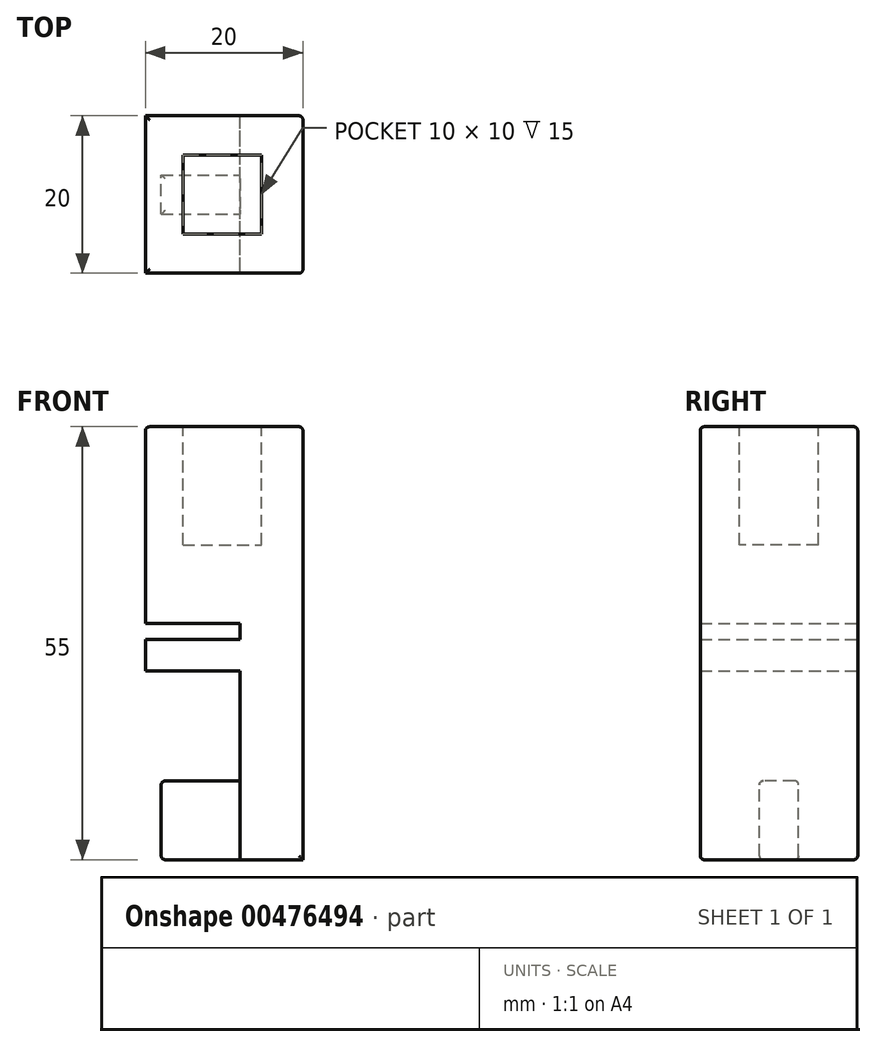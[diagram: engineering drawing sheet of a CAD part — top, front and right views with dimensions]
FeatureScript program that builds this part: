
annotation { "Feature Type Name" : "Feature", "Feature Type Description" : "" }
export const myFeature = defineFeature(function(context is Context, id is Id, definition is map)
    precondition{}
    {
        {
            var Q0;
            Q0=qCreatedBy(makeId("Front.planeOp"),FACE);
            var sketch = newSketch(context, id + "F0", { "sketchPlane" : qUnion([Q0])});
            skLineSegment(sketch, "E0.bottom", {"start": v(-17.88, 11) * mm, "end": v(2.12, 11) * mm});
            skLineSegment(sketch, "E0.top", {"start": v(-17.88, -24) * mm, "end": v(2.12, -24) * mm});
            skLineSegment(sketch, "E0.left", {"start": v(-17.88, 11) * mm, "end": v(-17.88, -24) * mm});
            skLineSegment(sketch, "E0.right", {"start": v(2.12, 11) * mm, "end": v(2.12, -24) * mm});
            skLineSegment(sketch, "E1", {"start": v(-17.88, 6) * mm, "end": v(2.12, 6) * mm});
            skLineSegment(sketch, "E2", {"start": v(-5.88, 6) * mm, "end": v(-5.88, -24) * mm});
            skLineSegment(sketch, "E3", {"start": v(-5.88, 4) * mm, "end": v(-17.88, 4) * mm});
            skLineSegment(sketch, "E4", {"start": v(-17.88, 0) * mm, "end": v(-5.88, 0) * mm});
            skLineSegment(sketch, "E5", {"start": v(-17.88, -14) * mm, "end": v(-5.88, -14) * mm});
            skSolve(sketch);
        }
        {
            var Q0;
            {var subQ1=sQuery(id+"F0.wireOp",EDGE,"E0.bottom");Q0=makeQuery(id+"F0.imprint","IMPRINT",FACE,{"disambiguationData":[TD([[makeQuery(id+"F0.imprint","IMPRINT",EDGE,{"derivedFrom":subQ1}),-1.0]])]});}
            var Q1;
            {var subQ1=sQuery(id+"F0.wireOp",EDGE,"E0.right");var subQ5=sQuery(id+"F0.wireOp",EDGE,"E0.top");var subQ6=makeQuery(id+"F0.imprint","INTERSECT",VERTEX,{"derivedFrom":[subQ5,subQ1]});Q1=makeQuery(id+"F0.imprint","IMPRINT",FACE,{"disambiguationData":[TD([[makeQuery(id+"F0.imprint","IMPRINT",EDGE,{"disambiguationData":[TD([[subQ6,1.0]])],"derivedFrom":subQ5}),1.0]])]});}
            var Q2;
            {var subQ0=sQuery(id+"F0.wireOp",EDGE,"E3");Q2=makeQuery(id+"F0.imprint","IMPRINT",FACE,{"disambiguationData":[TD([[makeQuery(id+"F0.imprint","IMPRINT",EDGE,{"derivedFrom":subQ0}),1.0]])]});}
            extrude(context, id + "F1", {"entities" : qUnion([Q0, Q1, Q2]), "depth" : 20 * mm});
        }
        {
            var Q0;
            {var subQ0=sQuery(id+"F0.wireOp",EDGE,"E2");Q0=makeQuery(id+"F1.opExtrude","SWEPT_FACE",FACE,{"disambiguationData":[OSD([subQ0]),TDD([makeQuery(id+"F0.imprint","IMPRINT",EDGE,{"disambiguationData":[TD([[makeQuery(id+"F0.imprint","INTERSECT",VERTEX,{"derivedFrom":[subQ0,sQuery(id+"F0.wireOp",EDGE,"E4")]}),-1.0]])],"derivedFrom":subQ0}),makeQuery(id+"F0.imprint","IMPRINT",EDGE,{"disambiguationData":[TD([[makeQuery(id+"F0.imprint","INTERSECT",VERTEX,{"derivedFrom":[sQuery(id+"F0.wireOp",EDGE,"E0.top"),subQ0]}),1.0]])],"derivedFrom":subQ0})])]});}
            var sketch = newSketch(context, id + "F2", { "sketchPlane" : qUnion([Q0])});
            skLineSegment(sketch, "E6.bottom", {"start": v(7.5, -24) * mm, "end": v(12.5, -24) * mm});
            skLineSegment(sketch, "E6.top", {"start": v(7.5, -14) * mm, "end": v(12.5, -14) * mm});
            skLineSegment(sketch, "E6.left", {"start": v(7.5, -24) * mm, "end": v(7.5, -14) * mm});
            skLineSegment(sketch, "E6.right", {"start": v(12.5, -24) * mm, "end": v(12.5, -14) * mm});
            skSolve(sketch);
        }
        {
            var Q0;
            Q0=makeQuery(id+"F2.imprint","IMPRINT",FACE,{"disambiguationData":[TD([[makeQuery(id+"F2.imprint","IMPRINT",EDGE,{"derivedFrom":sQuery(id+"F2.wireOp",EDGE,"E6.bottom")}),-1.0]])]});
            extrude(context, id + "F3", {"entities" : qUnion([Q0]), "operationType" : NewBodyOperationType.ADD, "depth" : 10 * mm});
        }
        {
            var Q0;
            Q0=makeQuery(id+"F1.opExtrude","SWEPT_FACE",FACE,{"disambiguationData":[OSD([sQuery(id+"F0.wireOp",EDGE,"E0.bottom")])]});
            extrude(context, id + "F4", {"entities" : qUnion([Q0]), "operationType" : NewBodyOperationType.ADD, "depth" : 20 * mm});
        }
        {
            var Q0;
            Q0=makeQuery(id+"F1.opExtrude","CAP_EDGE",EDGE,{"disambiguationData":[OSD([sQuery(id+"F0.wireOp",EDGE,"E0.right")])],"isStart":false});
            var Q1;
            Q1=makeQuery(id+"F1.opExtrude","CAP_EDGE",EDGE,{"disambiguationData":[OSD([sQuery(id+"F0.wireOp",EDGE,"E0.right")])],"isStart":true});
            var Q2;
            Q2=makeQuery(id+"F1.opExtrude","CAP_EDGE",EDGE,{"disambiguationData":[OSD([sQuery(id+"F0.wireOp",EDGE,"E0.top")])],"isStart":false});
            var Q3;
            Q3=makeQuery(id+"F1.opExtrude","CAP_EDGE",EDGE,{"disambiguationData":[OSD([sQuery(id+"F0.wireOp",EDGE,"E0.top")])],"isStart":true});
            var Q4;
            Q4=makeQuery(id+"F3.opExtrude","SWEPT_EDGE",EDGE,{"disambiguationData":[OSD([sQuery(id+"F2.wireOp",EDGE,"E6.top"),sQuery(id+"F2.wireOp",EDGE,"E6.right")])]});
            var Q5;
            Q5=makeQuery(id+"F3.opExtrude","SWEPT_EDGE",EDGE,{"disambiguationData":[OSD([sQuery(id+"F2.wireOp",EDGE,"E6.top"),sQuery(id+"F2.wireOp",EDGE,"E6.left")])]});
            var Q6;
            Q6=makeQuery(id+"F3.opExtrude","CAP_EDGE",EDGE,{"disambiguationData":[OSD([sQuery(id+"F2.wireOp",EDGE,"E6.top")])],"isStart":false});
            var Q7;
            Q7=makeQuery(id+"F3.opExtrude","CAP_EDGE",EDGE,{"disambiguationData":[OSD([sQuery(id+"F2.wireOp",EDGE,"E6.bottom")])],"isStart":false});
            var Q8;
            Q8=makeQuery(id+"F3.opExtrude","SWEPT_EDGE",EDGE,{"disambiguationData":[OSD([sQuery(id+"F0.wireOp",EDGE,"E0.top"),sQuery(id+"F0.wireOp",EDGE,"E2"),sQuery(id+"F2.wireOp",EDGE,"E6.bottom"),sQuery(id+"F2.wireOp",EDGE,"E6.right")])]});
            var Q9;
            Q9=makeQuery(id+"F3.opExtrude","SWEPT_EDGE",EDGE,{"disambiguationData":[OSD([sQuery(id+"F0.wireOp",EDGE,"E0.top"),sQuery(id+"F0.wireOp",EDGE,"E2"),sQuery(id+"F2.wireOp",EDGE,"E6.bottom"),sQuery(id+"F2.wireOp",EDGE,"E6.left")])]});
            var Q10;
            {var subQ0=sQuery(id+"F0.wireOp",EDGE,"E0.bottom");Q10=makeQuery(id+"F4.opExtrude","CAP_EDGE",EDGE,{"disambiguationData":[OSD([subQ0]),TDD([makeQuery(id+"F1.opExtrude","CAP_EDGE",EDGE,{"disambiguationData":[OSD([subQ0])],"isStart":false})])],"isStart":false});}
            var Q11;
            Q11=makeQuery(id+"F4.opExtrude","CAP_EDGE",EDGE,{"disambiguationData":[OSD([sQuery(id+"F0.wireOp",EDGE,"E0.bottom"),sQuery(id+"F0.wireOp",EDGE,"E0.left")])],"isStart":false});
            var Q12;
            {var subQ0=sQuery(id+"F0.wireOp",EDGE,"E0.bottom");Q12=makeQuery(id+"F4.opExtrude","CAP_EDGE",EDGE,{"disambiguationData":[OSD([subQ0]),TDD([makeQuery(id+"F1.opExtrude","CAP_EDGE",EDGE,{"disambiguationData":[OSD([subQ0])],"isStart":true})])],"isStart":false});}
            var Q13;
            Q13=makeQuery(id+"F4.opExtrude","CAP_EDGE",EDGE,{"disambiguationData":[OSD([sQuery(id+"F0.wireOp",EDGE,"E0.bottom"),sQuery(id+"F0.wireOp",EDGE,"E0.right")])],"isStart":false});
            fillet(context, id + "F5", {"entities" : qUnion([Q0, Q1, Q2, Q3, Q4, Q5, Q6, Q7, Q8, Q9, Q10, Q11, Q12, Q13]), "radius" : 0.5 * mm, "tangentPropagation" : true, "allowEdgeOverflow" : false});
        }
        {
            var Q0;
            Q0=makeQuery(id+"F4.opExtrude","CAP_FACE",FACE,{"disambiguationData":[OSD([sQuery(id+"F0.wireOp",EDGE,"E0.bottom")])],"isStart":false});
            var sketch = newSketch(context, id + "F6", { "sketchPlane" : qUnion([Q0])});
            skLineSegment(sketch, "E7.bottom", {"start": v(-13.13, -5) * mm, "end": v(-3.13, -5) * mm});
            skLineSegment(sketch, "E7.top", {"start": v(-13.13, -15) * mm, "end": v(-3.13, -15) * mm});
            skLineSegment(sketch, "E7.left", {"start": v(-13.13, -5) * mm, "end": v(-13.13, -15) * mm});
            skLineSegment(sketch, "E7.right", {"start": v(-3.13, -5) * mm, "end": v(-3.13, -15) * mm});
            skSolve(sketch);
        }
        {
            var Q0;
            Q0=makeQuery(id+"F6.imprint","IMPRINT",FACE,{"disambiguationData":[TD([[makeQuery(id+"F6.imprint","IMPRINT",EDGE,{"derivedFrom":sQuery(id+"F6.wireOp",EDGE,"E7.bottom")}),-1.0]])]});
            extrude(context, id + "F7", {"entities" : qUnion([Q0]), "operationType" : NewBodyOperationType.REMOVE, "oppositeDirection" : true, "depth" : 15 * mm});
        }
    });
